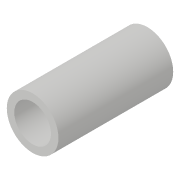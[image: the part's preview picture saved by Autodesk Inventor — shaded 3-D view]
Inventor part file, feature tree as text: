
AUTODESK INVENTOR PART (.ipt)
format: ipt  version: 2018 (Build 220112000, 112)  size: 104,960 bytes
history: native  units: in
note: dims shown in document units (in); Inventor stores cm internally (conversion verified against a paired STEP export)
features: extrude x1
ambient origin geometry x8: Origin, YZ Plane, XZ Plane, XY Plane, X Axis, Y Axis, Z Axis, Center Point
bodies: Solid1 (feature_tree)
feature tree (1):
  extrude  "Extrude1"  [1 undecoded]
note: 1 required parameter value undecoded (feature->parameter linkage not recoverable at this tier; creation-order binding heuristic only, values carry confidence <= 0.55)
